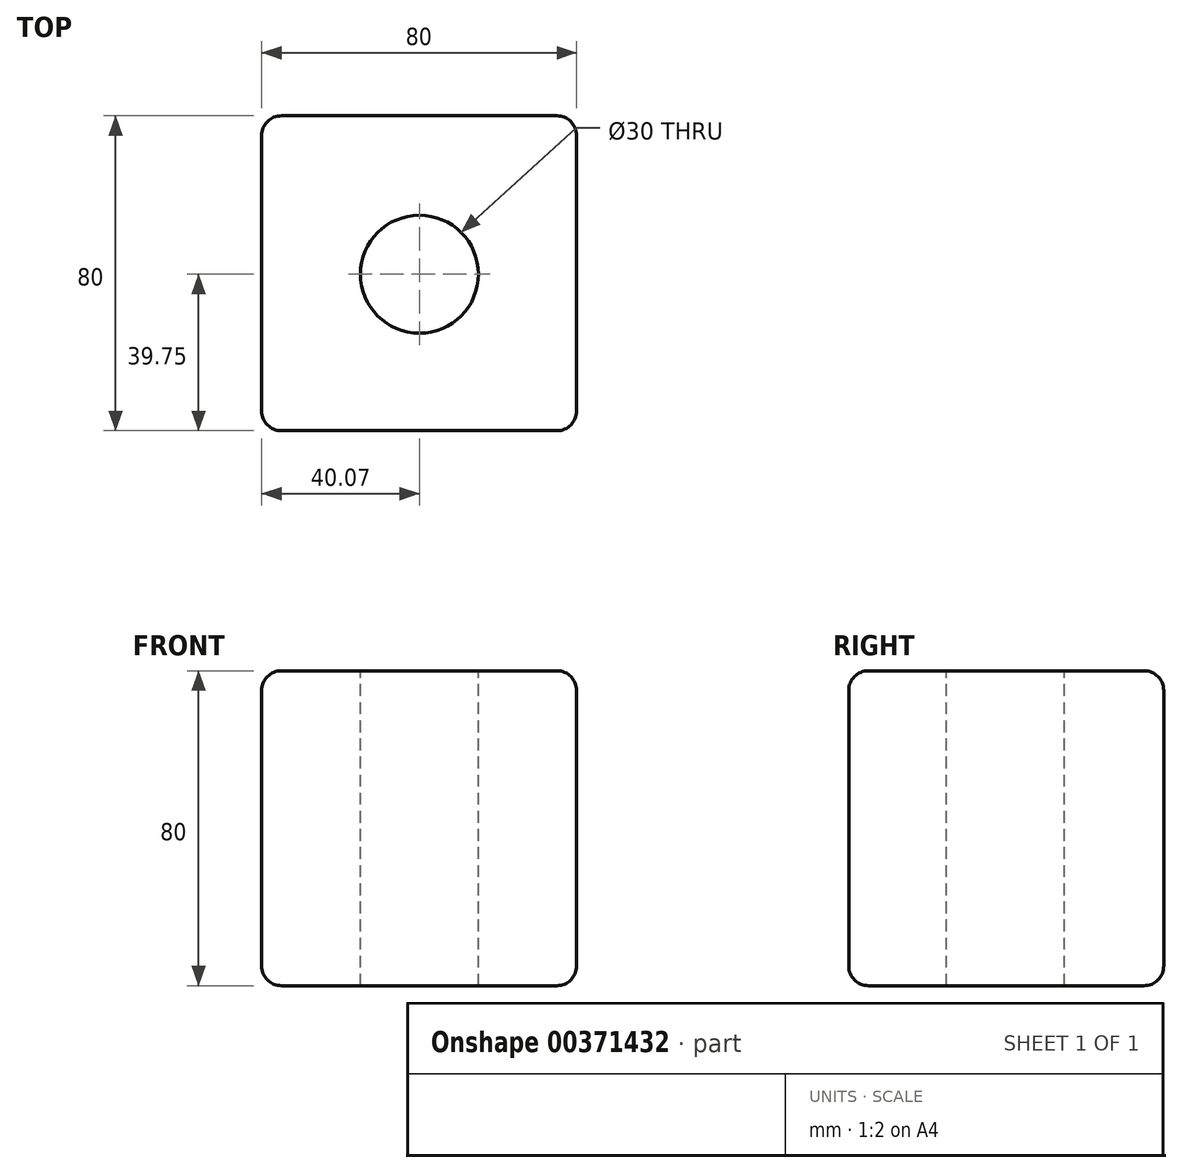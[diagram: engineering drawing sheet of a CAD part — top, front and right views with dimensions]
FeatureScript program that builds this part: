
annotation { "Feature Type Name" : "Feature", "Feature Type Description" : "" }
export const myFeature = defineFeature(function(context is Context, id is Id, definition is map)
    precondition{}
    {
        {
            var Q0;
            Q0=qCreatedBy(makeId("Top.planeOp"),FACE);
            var sketch = newSketch(context, id + "F0", { "sketchPlane" : qUnion([Q0])});
            skLineSegment(sketch, "E0.bottom", {"start": v(-57.17, 37.1) * mm, "end": v(22.83, 37.1) * mm});
            skLineSegment(sketch, "E0.top", {"start": v(-57.17, -42.9) * mm, "end": v(22.83, -42.9) * mm});
            skLineSegment(sketch, "E0.left", {"start": v(-57.17, 37.1) * mm, "end": v(-57.17, -42.9) * mm});
            skLineSegment(sketch, "E0.right", {"start": v(22.83, 37.1) * mm, "end": v(22.83, -42.9) * mm});
            skSolve(sketch);
        }
        {
            var Q0;
            Q0=makeQuery(id+"F0.imprint","IMPRINT",FACE,{"disambiguationData":[TD([[makeQuery(id+"F0.imprint","IMPRINT",EDGE,{"derivedFrom":sQuery(id+"F0.wireOp",EDGE,"E0.bottom")}),-1.0]])]});
            extrude(context, id + "F1", {"entities" : qUnion([Q0]), "depth" : 80 * mm});
        }
        {
            var Q0;
            Q0=makeQuery(id+"F1.opExtrude","CAP_FACE",FACE,{"disambiguationData":[OSD([sQuery(id+"F0.wireOp",EDGE,"E0.bottom"),sQuery(id+"F0.wireOp",EDGE,"E0.top"),sQuery(id+"F0.wireOp",EDGE,"E0.left"),sQuery(id+"F0.wireOp",EDGE,"E0.right")])],"isStart":false});
            var sketch = newSketch(context, id + "F2", { "sketchPlane" : qUnion([Q0])});
            skCircle(sketch, "E1", {"center": v(-17.1, -3.15) * mm, "radius": 15 * mm});
            skSolve(sketch);
        }
        {
            var Q0;
            Q0=makeQuery(id+"F2.imprint","IMPRINT",FACE,{"disambiguationData":[TD([[makeQuery(id+"F2.imprint","IMPRINT",EDGE,{"derivedFrom":sQuery(id+"F2.wireOp",EDGE,"E1")}),1.0]])]});
            extrude(context, id + "F3", {"entities" : qUnion([Q0]), "operationType" : NewBodyOperationType.REMOVE, "endBound" : BoundingType.THROUGH_ALL, "oppositeDirection" : true, "depth" : 25 * mm});
        }
        {
            var Q0;
            Q0=makeQuery(id+"F1.opExtrude","CAP_EDGE",EDGE,{"disambiguationData":[OSD([sQuery(id+"F0.wireOp",EDGE,"E0.bottom")])],"isStart":false});
            var Q1;
            Q1=makeQuery(id+"F1.opExtrude","CAP_EDGE",EDGE,{"disambiguationData":[OSD([sQuery(id+"F0.wireOp",EDGE,"E0.left")])],"isStart":false});
            var Q2;
            Q2=makeQuery(id+"F1.opExtrude","CAP_EDGE",EDGE,{"disambiguationData":[OSD([sQuery(id+"F0.wireOp",EDGE,"E0.top")])],"isStart":false});
            var Q3;
            Q3=makeQuery(id+"F1.opExtrude","CAP_EDGE",EDGE,{"disambiguationData":[OSD([sQuery(id+"F0.wireOp",EDGE,"E0.right")])],"isStart":false});
            var Q4;
            Q4=makeQuery(id+"F1.opExtrude","SWEPT_EDGE",EDGE,{"disambiguationData":[OSD([sQuery(id+"F0.wireOp",EDGE,"E0.bottom"),sQuery(id+"F0.wireOp",EDGE,"E0.left")])]});
            var Q5;
            Q5=makeQuery(id+"F1.opExtrude","SWEPT_EDGE",EDGE,{"disambiguationData":[OSD([sQuery(id+"F0.wireOp",EDGE,"E0.top"),sQuery(id+"F0.wireOp",EDGE,"E0.left")])]});
            var Q6;
            Q6=makeQuery(id+"F1.opExtrude","SWEPT_FACE",FACE,{"disambiguationData":[OSD([sQuery(id+"F0.wireOp",EDGE,"E0.left")])]});
            var Q7;
            Q7=makeQuery(id+"F1.opExtrude","SWEPT_EDGE",EDGE,{"disambiguationData":[OSD([sQuery(id+"F0.wireOp",EDGE,"E0.bottom"),sQuery(id+"F0.wireOp",EDGE,"E0.right")])]});
            var Q8;
            Q8=makeQuery(id+"F1.opExtrude","SWEPT_EDGE",EDGE,{"disambiguationData":[OSD([sQuery(id+"F0.wireOp",EDGE,"E0.top"),sQuery(id+"F0.wireOp",EDGE,"E0.right")])]});
            var Q9;
            Q9=makeQuery(id+"F1.opExtrude","SWEPT_FACE",FACE,{"disambiguationData":[OSD([sQuery(id+"F0.wireOp",EDGE,"E0.right")])]});
            var Q10;
            Q10=makeQuery(id+"F1.opExtrude","CAP_EDGE",EDGE,{"disambiguationData":[OSD([sQuery(id+"F0.wireOp",EDGE,"E0.bottom")])],"isStart":true});
            var Q11;
            Q11=makeQuery(id+"F1.opExtrude","CAP_EDGE",EDGE,{"disambiguationData":[OSD([sQuery(id+"F0.wireOp",EDGE,"E0.top")])],"isStart":true});
            fillet(context, id + "F4", {"entities" : qUnion([Q0, Q1, Q2, Q3, Q4, Q5, Q6, Q7, Q8, Q9, Q10, Q11]), "radius" : 5 * mm, "tangentPropagation" : true, "allowEdgeOverflow" : false});
        }
    });
